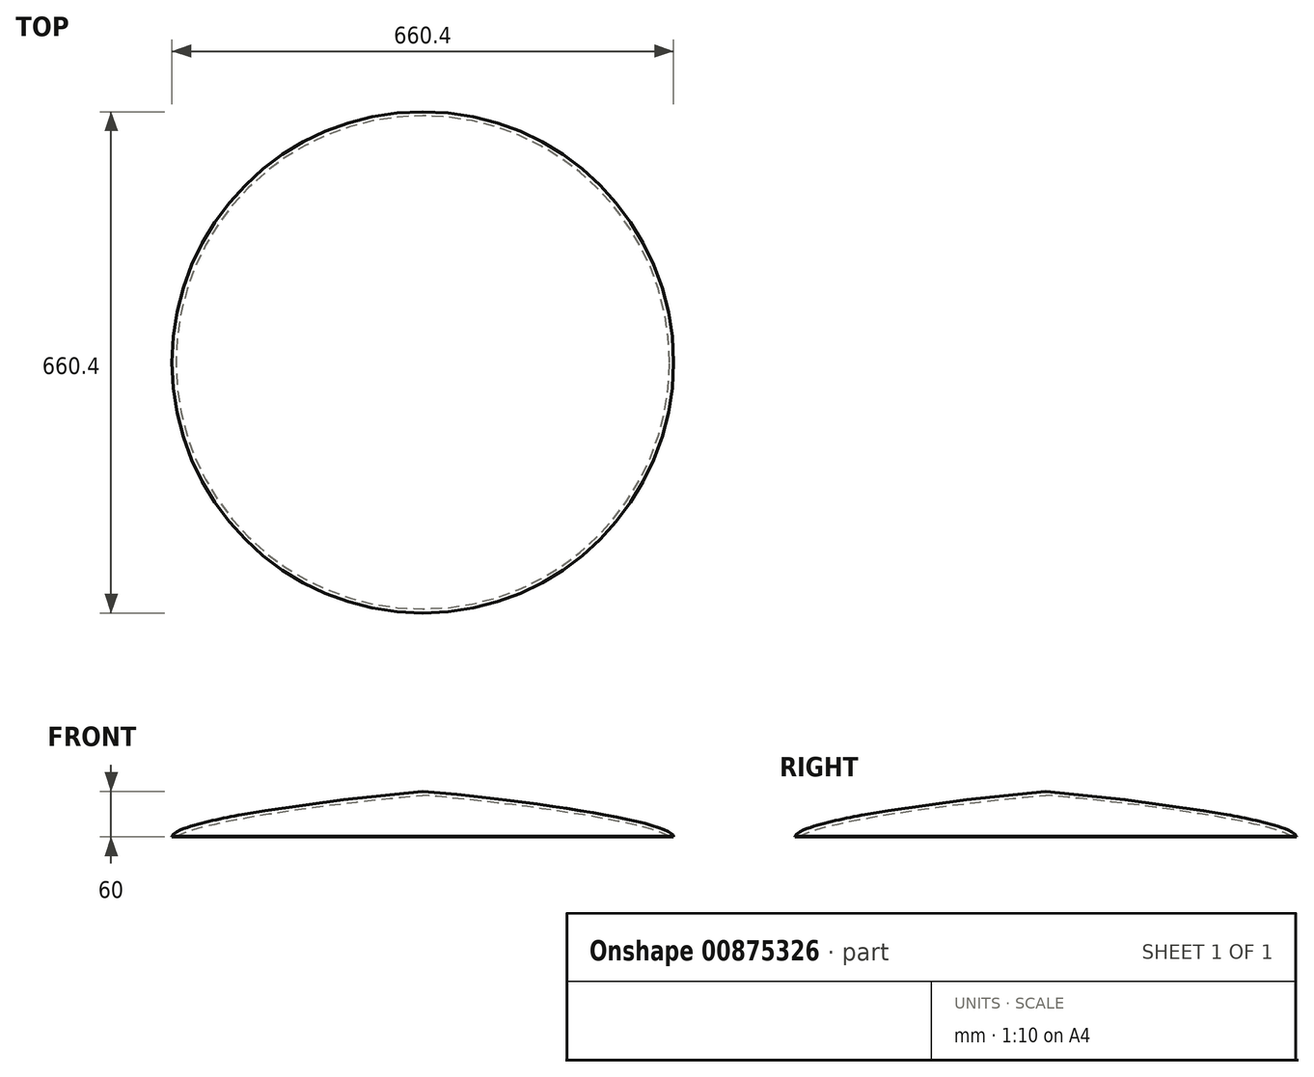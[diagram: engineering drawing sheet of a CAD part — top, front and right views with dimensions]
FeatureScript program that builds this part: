
annotation { "Feature Type Name" : "Feature", "Feature Type Description" : "" }
export const myFeature = defineFeature(function(context is Context, id is Id, definition is map)
    precondition{}
    {
        {
            var Q0;
            Q0=qCreatedBy(makeId("Front.planeOp"),FACE);
            var sketch = newSketch(context, id + "F0", { "sketchPlane" : qUnion([Q0])});
            skLineSegment(sketch, "E0", {"start": v(0, 0) * mm, "end": v(330.2, 0) * mm});
            skLineSegment(sketch, "E1", {"start": v(0, 0) * mm, "end": v(0, 60) * mm});
            skLineSegment(sketch, "E2", {"start": v(330.2, 0) * mm, "end": v(330.2, 0.53) * mm});
            skLineSegment(sketch, "E3", {"start": v(330.2, 0.53) * mm, "end": v(330.2, 0.54) * mm});
            skPoint(sketch, "E4.visualSharp", {"position": v(330.2, 0) * mm});
            skLineSegment(sketch, "E4.filletArc", {"start": v(330.2, 0) * mm, "end": v(330.2, 0) * mm});
            skPoint(sketch, "E5.visualSharp", {"position": v(330.2, 0.53) * mm});
            skLineSegment(sketch, "E5.filletArc", {"start": v(330.2, 0.53) * mm, "end": v(330.2, 0.53) * mm});
            skLineSegment(sketch, "E6", {"start": v(0, 60) * mm, "end": v(0, -34.26) * mm, "construction": true});
            skPoint(sketch, "E7", {"position": v(0, 30) * mm});
            skEllipticalArc(sketch, "E8", {});
            const initialGuessF0  = {"E8": [0, 0.03, 0.9958981493191077, -0.09048135820585476, 0.3315600096513449, 0.029877945780137635, 0, 1.5789832944345814]};
            skSetInitialGuess(sketch, initialGuessF0);
            skSolve(sketch);
        }
        {
            var Q0;
            Q0=makeQuery(id+"F0.imprint","IMPRINT",FACE,{"disambiguationData":[TD([[makeQuery(id+"F0.imprint","IMPRINT",EDGE,{"derivedFrom":sQuery(id+"F0.wireOp",EDGE,"E0")}),1.0]])]});
            var Q1;
            Q1=sQuery(id+"F0.wireOp",EDGE,"E6");
            revolve(context, id + "F1", {"surfaceOperationType" : NewSurfaceOperationType.NEW, "entities" : qUnion([Q0]), "axis" : qUnion([Q1]), "revolveType" : RevolveType.FULL});
        }
        {
            var Q0;
            Q0=makeQuery(id+"F1.opRevolve","SWEPT_FACE",FACE,{"disambiguationData":[OSD([sQuery(id+"F0.wireOp",EDGE,"E0")])]});
            shell(context, id + "F2", {"entities" : qUnion([Q0]), "thickness" : 5 * mm});
        }
        {
            var Q0;
            Q0=makeQuery(id+"F1.opRevolve","SWEPT_FACE",FACE,{"disambiguationData":[OSD([sQuery(id+"F0.wireOp",EDGE,"E0")])]});
            cPlane(context, id + "F3", {"entities" : qUnion([Q0]), "cplaneType" : CPlaneType.OFFSET, "offset" : 60 * mm, "oppositeDirection" : true, "width" : 150 * mm, "height" : 150 * mm});
        }
    });
